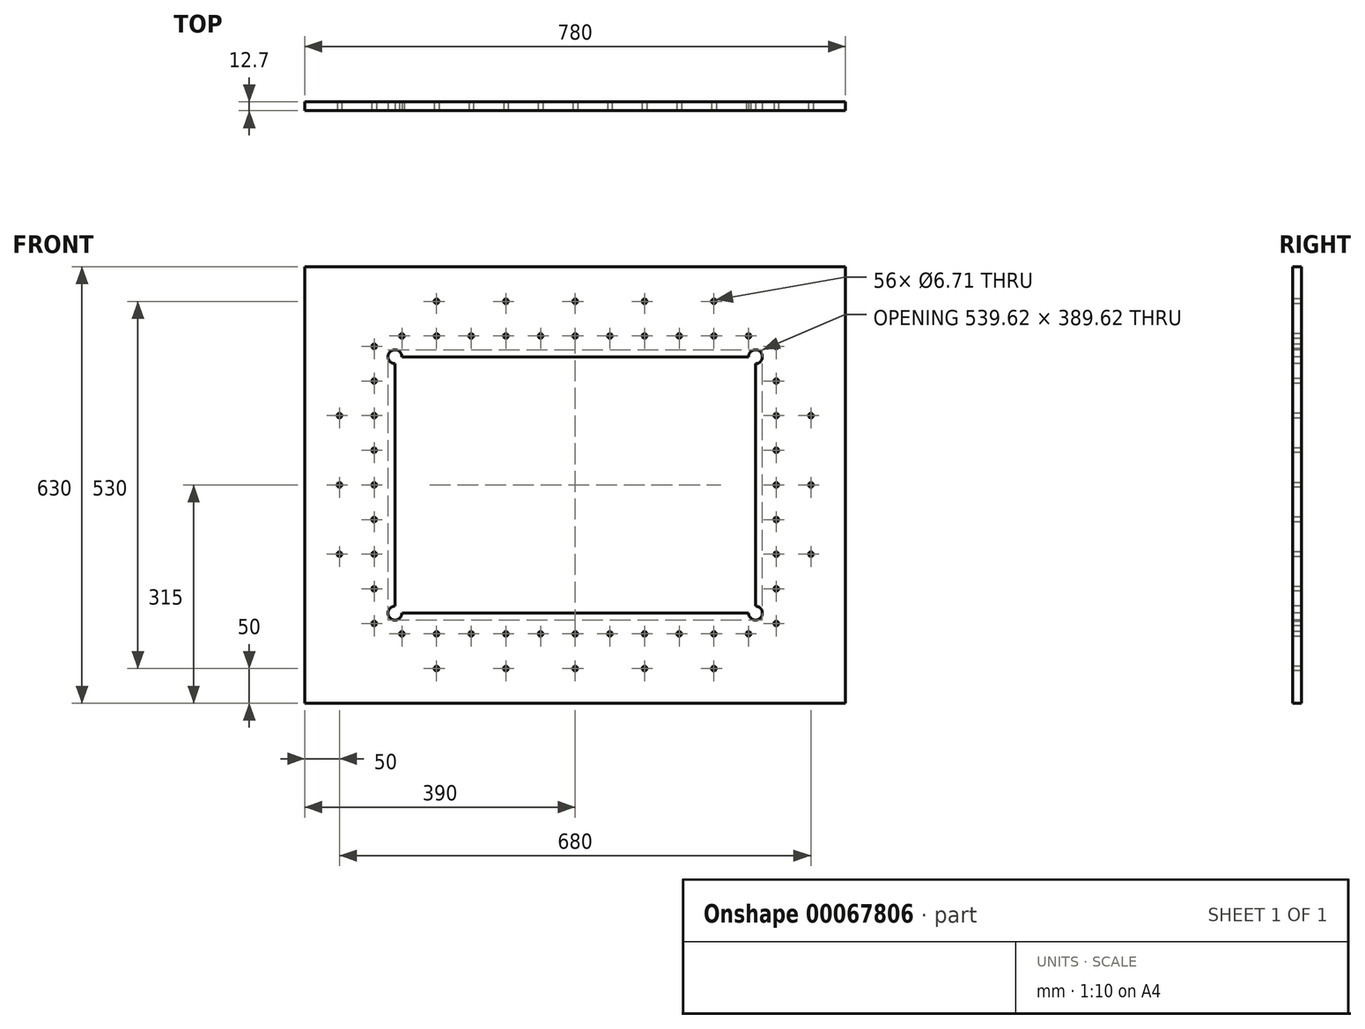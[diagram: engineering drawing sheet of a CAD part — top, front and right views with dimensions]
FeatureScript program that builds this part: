
annotation { "Feature Type Name" : "Feature", "Feature Type Description" : "" }
export const myFeature = defineFeature(function(context is Context, id is Id, definition is map)
    precondition{}
    {
        {
            var Q0;
            Q0=qCreatedBy(makeId("Front.planeOp"),FACE);
            var sketch = newSketch(context, id + "F0", { "sketchPlane" : qUnion([Q0])});
            skLineSegment(sketch, "E0.rect.bottom", {"start": v(390, -315) * mm, "end": v(-390, -315) * mm});
            skLineSegment(sketch, "E0.rect.top", {"start": v(390, 315) * mm, "end": v(-390, 315) * mm});
            skLineSegment(sketch, "E0.rect.left", {"start": v(390, -315) * mm, "end": v(390, 315) * mm});
            skLineSegment(sketch, "E0.rect.right", {"start": v(-390, -315) * mm, "end": v(-390, 315) * mm});
            skPoint(sketch, "E0.rect.middle", {"position": v(0, 0) * mm});
            skLineSegment(sketch, "E1.rect.bottom", {"start": v(260, -185) * mm, "end": v(-260, -185) * mm});
            skLineSegment(sketch, "E1.rect.top", {"start": v(260, 185) * mm, "end": v(-260, 185) * mm});
            skLineSegment(sketch, "E1.rect.left", {"start": v(260, -185) * mm, "end": v(260, 185) * mm});
            skLineSegment(sketch, "E1.rect.right", {"start": v(-260, -185) * mm, "end": v(-260, 185) * mm});
            skSolve(sketch);
        }
        {
            var Q0;
            Q0 = qSketchRegion(id + "F0", true);
            extrude(context, id + "F1", {"entities" : qUnion([Q0]), "oppositeDirection" : true, "depth" : 12.7 * mm});
        }
        {
            var Q0;
            Q0=makeQuery(id+"F1.opExtrude","CAP_FACE",FACE,{"disambiguationData":[OSD([sQuery(id+"F0.wireOp",EDGE,"E0.rect.bottom"),sQuery(id+"F0.wireOp",EDGE,"E0.rect.top"),sQuery(id+"F0.wireOp",EDGE,"E0.rect.left"),sQuery(id+"F0.wireOp",EDGE,"E0.rect.right"),sQuery(id+"F0.wireOp",EDGE,"E1.rect.bottom"),sQuery(id+"F0.wireOp",EDGE,"E1.rect.top"),sQuery(id+"F0.wireOp",EDGE,"E1.rect.left"),sQuery(id+"F0.wireOp",EDGE,"E1.rect.right")])],"isStart":true});
            var sketch = newSketch(context, id + "F2", { "sketchPlane" : qUnion([Q0])});
            skLineSegment(sketch, "E2", {"start": v(0, 315) * mm, "end": v(0, -315) * mm, "construction": true});
            skLineSegment(sketch, "E3", {"start": v(-390, 0) * mm, "end": v(390, 0) * mm, "construction": true});
            skPoint(sketch, "E4", {"position": v(0, 215) * mm});
            skPoint(sketch, "E5", {"position": v(-50, 215) * mm});
            skPoint(sketch, "E6", {"position": v(-100, 215) * mm});
            skPoint(sketch, "E7", {"position": v(-150, 215) * mm});
            skPoint(sketch, "E8", {"position": v(-200, 215) * mm});
            skPoint(sketch, "E9", {"position": v(-250, 215) * mm});
            skPoint(sketch, "E10", {"position": v(50, 215) * mm});
            skPoint(sketch, "E11", {"position": v(100, 215) * mm});
            skPoint(sketch, "E12", {"position": v(150, 215) * mm});
            skPoint(sketch, "E13", {"position": v(200, 215) * mm});
            skPoint(sketch, "E14", {"position": v(250, 215) * mm});
            skPoint(sketch, "E15", {"position": v(0, 265) * mm});
            skPoint(sketch, "E16", {"position": v(100, 265) * mm});
            skPoint(sketch, "E17", {"position": v(200, 265) * mm});
            skPoint(sketch, "E18", {"position": v(-100, 265) * mm});
            skPoint(sketch, "E19", {"position": v(-200, 265) * mm});
            skPoint(sketch, "E20.MirrorP", {"position": v(-250, -215) * mm});
            skPoint(sketch, "E21.MirrorP", {"position": v(-200, -215) * mm});
            skPoint(sketch, "E22.MirrorP", {"position": v(-150, -215) * mm});
            skPoint(sketch, "E23.MirrorP", {"position": v(-100, -215) * mm});
            skPoint(sketch, "E24.MirrorP", {"position": v(-50, -215) * mm});
            skPoint(sketch, "E25.MirrorP", {"position": v(0, -215) * mm});
            skPoint(sketch, "E26.MirrorP", {"position": v(50, -215) * mm});
            skPoint(sketch, "E27.MirrorP", {"position": v(100, -215) * mm});
            skPoint(sketch, "E28.MirrorP", {"position": v(150, -215) * mm});
            skPoint(sketch, "E29.MirrorP", {"position": v(200, -215) * mm});
            skPoint(sketch, "E30.MirrorP", {"position": v(250, -215) * mm});
            skPoint(sketch, "E31.MirrorP", {"position": v(200, -265) * mm});
            skPoint(sketch, "E32.MirrorP", {"position": v(100, -265) * mm});
            skPoint(sketch, "E33.MirrorP", {"position": v(0, -265) * mm});
            skPoint(sketch, "E34.MirrorP", {"position": v(-100, -265) * mm});
            skPoint(sketch, "E35.MirrorP", {"position": v(-200, -265) * mm});
            skSolve(sketch);
        }
        {
            var Q0;
            Q0=makeQuery(id+"F1.opExtrude","CAP_FACE",FACE,{"disambiguationData":[OSD([sQuery(id+"F0.wireOp",EDGE,"E0.rect.bottom"),sQuery(id+"F0.wireOp",EDGE,"E0.rect.top"),sQuery(id+"F0.wireOp",EDGE,"E0.rect.left"),sQuery(id+"F0.wireOp",EDGE,"E0.rect.right"),sQuery(id+"F0.wireOp",EDGE,"E1.rect.bottom"),sQuery(id+"F0.wireOp",EDGE,"E1.rect.top"),sQuery(id+"F0.wireOp",EDGE,"E1.rect.left"),sQuery(id+"F0.wireOp",EDGE,"E1.rect.right")])],"isStart":true});
            var sketch = newSketch(context, id + "F3", { "sketchPlane" : qUnion([Q0])});
            skLineSegment(sketch, "E36", {"start": v(-390, 0) * mm, "end": v(390, 0) * mm, "construction": true});
            skLineSegment(sketch, "E37", {"start": v(0, 315) * mm, "end": v(0, -315) * mm, "construction": true});
            skPoint(sketch, "E38", {"position": v(-290, 0) * mm});
            skPoint(sketch, "E39", {"position": v(-340, 0) * mm});
            skPoint(sketch, "E40", {"position": v(-290, 50) * mm});
            skPoint(sketch, "E41", {"position": v(-290, 100) * mm});
            skPoint(sketch, "E42", {"position": v(-290, 150) * mm});
            skPoint(sketch, "E43", {"position": v(-290, 200) * mm});
            skPoint(sketch, "E44", {"position": v(-290, -100) * mm});
            skPoint(sketch, "E45", {"position": v(-290, -200) * mm});
            skPoint(sketch, "E46", {"position": v(-290, -50) * mm});
            skPoint(sketch, "E47", {"position": v(-290, -150) * mm});
            skPoint(sketch, "E48", {"position": v(-340, 100) * mm});
            skPoint(sketch, "E49", {"position": v(-340, -100) * mm});
            skPoint(sketch, "E50.MirrorP", {"position": v(290, 200) * mm});
            skPoint(sketch, "E51.MirrorP", {"position": v(290, 150) * mm});
            skPoint(sketch, "E52.MirrorP", {"position": v(290, 100) * mm});
            skPoint(sketch, "E53.MirrorP", {"position": v(290, 50) * mm});
            skPoint(sketch, "E54.MirrorP", {"position": v(290, 0) * mm});
            skPoint(sketch, "E55.MirrorP", {"position": v(290, -50) * mm});
            skPoint(sketch, "E56.MirrorP", {"position": v(290, -100) * mm});
            skPoint(sketch, "E57.MirrorP", {"position": v(290, -150) * mm});
            skPoint(sketch, "E58.MirrorP", {"position": v(290, -200) * mm});
            skPoint(sketch, "E59.MirrorP", {"position": v(340, -100) * mm});
            skPoint(sketch, "E60.MirrorP", {"position": v(340, 0) * mm});
            skPoint(sketch, "E61.MirrorP", {"position": v(340, 100) * mm});
            skSolve(sketch);
        }
        {
            var Q0;
            Q0=sQuery(id+"F2.wireOp",VERTEX,"E9");
            var Q1;
            Q1=sQuery(id+"F2.wireOp",VERTEX,"E8");
            var Q2;
            Q2=sQuery(id+"F2.wireOp",VERTEX,"E7");
            var Q3;
            Q3=sQuery(id+"F2.wireOp",VERTEX,"E6");
            var Q4;
            Q4=sQuery(id+"F2.wireOp",VERTEX,"E5");
            var Q5;
            Q5=sQuery(id+"F2.wireOp",VERTEX,"E4");
            var Q6;
            Q6=sQuery(id+"F2.wireOp",VERTEX,"E10");
            var Q7;
            Q7=sQuery(id+"F2.wireOp",VERTEX,"E11");
            var Q8;
            Q8=sQuery(id+"F2.wireOp",VERTEX,"E12");
            var Q9;
            Q9=sQuery(id+"F2.wireOp",VERTEX,"E13");
            var Q10;
            Q10=sQuery(id+"F2.wireOp",VERTEX,"E14");
            var Q11;
            Q11=sQuery(id+"F2.wireOp",VERTEX,"E17");
            var Q12;
            Q12=sQuery(id+"F2.wireOp",VERTEX,"E16");
            var Q13;
            Q13=sQuery(id+"F2.wireOp",VERTEX,"E15");
            var Q14;
            Q14=sQuery(id+"F2.wireOp",VERTEX,"E18");
            var Q15;
            Q15=sQuery(id+"F2.wireOp",VERTEX,"E19");
            var Q16;
            Q16=sQuery(id+"F3.wireOp",VERTEX,"E43");
            var Q17;
            Q17=sQuery(id+"F3.wireOp",VERTEX,"E42");
            var Q18;
            Q18=sQuery(id+"F3.wireOp",VERTEX,"E41");
            var Q19;
            Q19=sQuery(id+"F3.wireOp",VERTEX,"E40");
            var Q20;
            Q20=sQuery(id+"F3.wireOp",VERTEX,"E38");
            var Q21;
            Q21=sQuery(id+"F3.wireOp",VERTEX,"E39");
            var Q22;
            Q22=sQuery(id+"F3.wireOp",VERTEX,"E48");
            var Q23;
            Q23=sQuery(id+"F3.wireOp",VERTEX,"E46");
            var Q24;
            Q24=sQuery(id+"F3.wireOp",VERTEX,"E44");
            var Q25;
            Q25=sQuery(id+"F3.wireOp",VERTEX,"E47");
            var Q26;
            Q26=sQuery(id+"F2.wireOp",VERTEX,"E32.MirrorP");
            var Q27;
            Q27=sQuery(id+"F2.wireOp",VERTEX,"E33.MirrorP");
            var Q28;
            Q28=sQuery(id+"F2.wireOp",VERTEX,"E31.MirrorP");
            var Q29;
            Q29=sQuery(id+"F2.wireOp",VERTEX,"E34.MirrorP");
            var Q30;
            Q30=sQuery(id+"F2.wireOp",VERTEX,"E35.MirrorP");
            var Q31;
            Q31=sQuery(id+"F2.wireOp",VERTEX,"E27.MirrorP");
            var Q32;
            Q32=sQuery(id+"F2.wireOp",VERTEX,"E23.MirrorP");
            var Q33;
            Q33=sQuery(id+"F2.wireOp",VERTEX,"E21.MirrorP");
            var Q34;
            Q34=sQuery(id+"F2.wireOp",VERTEX,"E30.MirrorP");
            var Q35;
            Q35=sQuery(id+"F2.wireOp",VERTEX,"E28.MirrorP");
            var Q36;
            Q36=sQuery(id+"F2.wireOp",VERTEX,"E24.MirrorP");
            var Q37;
            Q37=sQuery(id+"F2.wireOp",VERTEX,"E22.MirrorP");
            var Q38;
            Q38=sQuery(id+"F2.wireOp",VERTEX,"E25.MirrorP");
            var Q39;
            Q39=sQuery(id+"F2.wireOp",VERTEX,"E26.MirrorP");
            var Q40;
            Q40=sQuery(id+"F2.wireOp",VERTEX,"E20.MirrorP");
            var Q41;
            Q41=sQuery(id+"F2.wireOp",VERTEX,"E29.MirrorP");
            var Q42;
            Q42=sQuery(id+"F3.wireOp",VERTEX,"E45");
            var Q43;
            Q43=sQuery(id+"F3.wireOp",VERTEX,"E53.MirrorP");
            var Q44;
            Q44=sQuery(id+"F3.wireOp",VERTEX,"E54.MirrorP");
            var Q45;
            Q45=sQuery(id+"F3.wireOp",VERTEX,"E50.MirrorP");
            var Q46;
            Q46=sQuery(id+"F3.wireOp",VERTEX,"E51.MirrorP");
            var Q47;
            Q47=sQuery(id+"F3.wireOp",VERTEX,"E52.MirrorP");
            var Q48;
            Q48=sQuery(id+"F3.wireOp",VERTEX,"E58.MirrorP");
            var Q49;
            Q49=sQuery(id+"F3.wireOp",VERTEX,"E57.MirrorP");
            var Q50;
            Q50=sQuery(id+"F3.wireOp",VERTEX,"E56.MirrorP");
            var Q51;
            Q51=sQuery(id+"F3.wireOp",VERTEX,"E55.MirrorP");
            var Q52;
            Q52=sQuery(id+"F3.wireOp",VERTEX,"E49");
            var Q53;
            Q53=sQuery(id+"F3.wireOp",VERTEX,"E61.MirrorP");
            var Q54;
            Q54=sQuery(id+"F3.wireOp",VERTEX,"E60.MirrorP");
            var Q55;
            Q55=sQuery(id+"F3.wireOp",VERTEX,"E59.MirrorP");
            var Q56;
            Q56=sQuery(id+"F3.wireOp",VERTEX,"E60.MirrorP");
            var Q57;
            Q57=sQuery(id+"F3.wireOp",VERTEX,"E59.MirrorP");
            var Q58;
            Q58=makeQuery(id+"F1.opExtrude","SWEPT_BODY",BODY,{"disambiguationData":[OSD([sQuery(id+"F0.wireOp",EDGE,"E0.rect.bottom"),sQuery(id+"F0.wireOp",EDGE,"E0.rect.top"),sQuery(id+"F0.wireOp",EDGE,"E0.rect.left"),sQuery(id+"F0.wireOp",EDGE,"E0.rect.right"),sQuery(id+"F0.wireOp",EDGE,"E1.rect.bottom"),sQuery(id+"F0.wireOp",EDGE,"E1.rect.top"),sQuery(id+"F0.wireOp",EDGE,"E1.rect.left"),sQuery(id+"F0.wireOp",EDGE,"E1.rect.right")])]});
            hole(context, id + "F4", {"style" : HoleStyle.SIMPLE, "holeDiameter" : 6.7 * mm, "endStyle" : HoleEndStyle.THROUGH, "locations" : qUnion([Q0, Q1, Q2, Q3, Q4, Q5, Q6, Q7, Q8, Q9, Q10, Q11, Q12, Q13, Q14, Q15, Q16, Q17, Q18, Q19, Q20, Q21, Q22, Q23, Q24, Q25, Q26, Q27, Q28, Q29, Q30, Q31, Q32, Q33, Q34, Q35, Q36, Q37, Q38, Q39, Q40, Q41, Q42, Q43, Q44, Q45, Q46, Q47, Q48, Q49, Q50, Q51, Q52, Q53, Q54, Q55, Q56, Q57]), "scope" : qUnion([Q58])});
        }
        {
            var Q0;
            Q0=makeQuery(id+"F1.opExtrude","CAP_FACE",FACE,{"disambiguationData":[OSD([sQuery(id+"F0.wireOp",EDGE,"E0.rect.bottom"),sQuery(id+"F0.wireOp",EDGE,"E0.rect.top"),sQuery(id+"F0.wireOp",EDGE,"E0.rect.left"),sQuery(id+"F0.wireOp",EDGE,"E0.rect.right"),sQuery(id+"F0.wireOp",EDGE,"E1.rect.bottom"),sQuery(id+"F0.wireOp",EDGE,"E1.rect.top"),sQuery(id+"F0.wireOp",EDGE,"E1.rect.left"),sQuery(id+"F0.wireOp",EDGE,"E1.rect.right")])],"isStart":true});
            var sketch = newSketch(context, id + "F5", { "sketchPlane" : qUnion([Q0])});
            skCircle(sketch, "E62", {"center": v(-260, 185) * mm, "radius": 10 * mm});
            skCircle(sketch, "E63", {"center": v(-260, -185) * mm, "radius": 10 * mm});
            skCircle(sketch, "E64", {"center": v(260, -185) * mm, "radius": 10 * mm});
            skCircle(sketch, "E65", {"center": v(260, 185) * mm, "radius": 10 * mm});
            skSolve(sketch);
        }
        {
            var Q0;
            Q0 = qSketchRegion(id + "F5", true);
            extrude(context, id + "F6", {"entities" : qUnion([Q0]), "operationType" : NewBodyOperationType.REMOVE, "endBound" : BoundingType.THROUGH_ALL, "oppositeDirection" : true, "depth" : 25.4 * mm});
        }
    });
